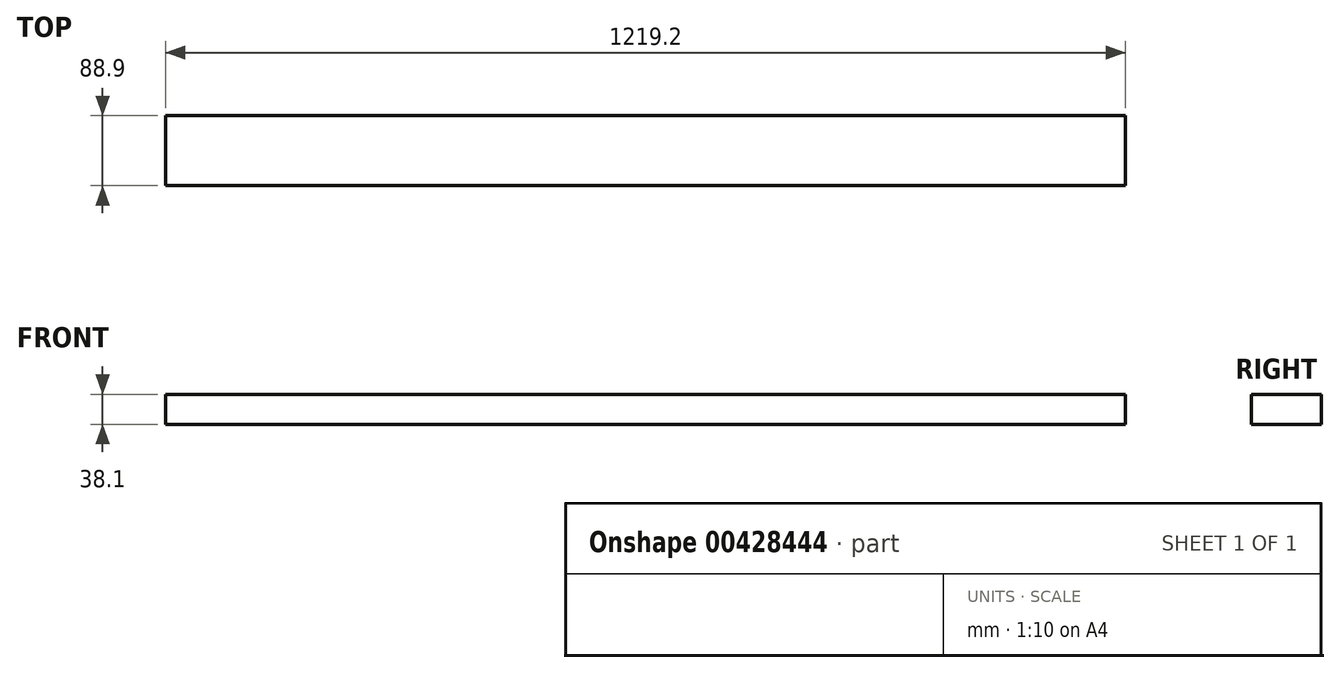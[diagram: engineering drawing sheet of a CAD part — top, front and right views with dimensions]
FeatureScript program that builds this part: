
annotation { "Feature Type Name" : "Feature", "Feature Type Description" : "" }
export const myFeature = defineFeature(function(context is Context, id is Id, definition is map)
    precondition{}
    {
        {
            var Q0;
            Q0=qCreatedBy(makeId("Right.planeOp"),FACE);
            var sketch = newSketch(context, id + "F0", { "sketchPlane" : qUnion([Q0])});
            skLineSegment(sketch, "E0.bottom", {"start": v(44.45, -19.05) * mm, "end": v(-44.45, -19.05) * mm});
            skLineSegment(sketch, "E0.top", {"start": v(44.45, 19.05) * mm, "end": v(-44.45, 19.05) * mm});
            skLineSegment(sketch, "E0.left", {"start": v(44.45, -19.05) * mm, "end": v(44.45, 19.05) * mm});
            skLineSegment(sketch, "E0.right", {"start": v(-44.45, -19.05) * mm, "end": v(-44.45, 19.05) * mm});
            skPoint(sketch, "E0.middle", {"position": v(0, 0) * mm});
            skSolve(sketch);
        }
        {
            var Q0;
            Q0=makeQuery(id+"F0.imprint","IMPRINT",FACE,{"disambiguationData":[TD([[makeQuery(id+"F0.imprint","IMPRINT",EDGE,{"derivedFrom":sQuery(id+"F0.wireOp",EDGE,"E0.bottom")}),-1.0]])]});
            extrude(context, id + "F1", {"entities" : qUnion([Q0]), "depth" : 609.6 * mm, "hasSecondDirection" : true, "secondDirectionOppositeDirection" : true, "secondDirectionDepth" : 609.6 * mm});
        }
    });
